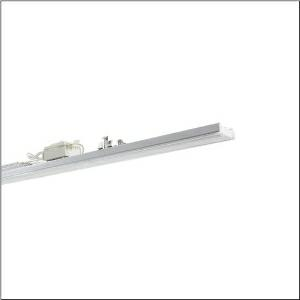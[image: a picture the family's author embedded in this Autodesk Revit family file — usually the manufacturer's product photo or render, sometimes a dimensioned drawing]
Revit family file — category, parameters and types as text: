
# Revit family: licross_21_recessed_mo_52te147n48xg
name_source: partatom
category: Lighting Fixtures
units: mm (PartAtom-declared; Revit-internal decimal feet)

## family parameters
Cut with Voids When Loaded = No
Host = Face
Light Source = No
Part Type = Normal
Room Calculation Point = No
Round Connector Dimension = Use Diameter
Shared = No

## types (1)
- Licross 21 Recessed MO (1 x LED, 8120 lm, 47.9 W, 4000K)
    Apparent Load = 48 VA
    CIE Flux Codes = 56 84 97 100 100
    Color Rendering = 80
    Color Temperature = 4000K
    Default Elevation = 1800 mm
    Description = Licross 21 Recessed MO, luminaire insert, of sheet steel, galvanised, coil coated, white, length: 1.500mm, width: 66mm, height: 67mm, LED rated luminous flux: 8.120lm, light colour: 840, SDCM (Standard Deviation of Colour Matching)MacAdam ≤ 3 SDCM (initial), control gear: ON/OFF, with plug, 3-pole, with phase selection, mains connection: 220..240V, AC, 50/60Hz, rated input power: 48W, internal wiring halogen-free, primary light control with lens, of plastic, primary optical cover: cover, of PMMA, light emission: direct distribution, primary light characteristic: asymmetric, protection rating (complete): IP54, insulation class (complete): insulation class I (protective earthing), certification: CE, ENEC, VDE, UKCA, protection symbol: D if used in an environment with non-conductive dust loads with corresponding accessories, impact resistance: IK06, permissible ambient temperature for indoor applications: -35..+40°C, corresponds to IFS (International Featured Standards) requirements for safety and quality in the food industry, reducing of maximum allowable ambient temperature of 5°C with ceiling mounting, LABS conformity tested according to VDMA 24364:2018-05, The light source and the operating device comply with the requirements of the Ecodesign Regulation (EU) 2019/2020 and are replaceable in accordance with this regulation, packaging unit: 1 piece
    Height = 58 mm
    Lamp = 1 x LED
    Lamp Light Flux = 8120 lm
    Lamp Power = 47.9 W
    Lamp count = 1
    Length = 1500 mm
    Luminous efficacy = 170 lm/W
    Manufacturer = Siteco
    ModVariant = No
    Model = 52TE147N48XG
    Mounting Place = Ceiling
    Mounting Type = Pendant
    Number of Poles = 1
    OnlyDefault = Yes
    Power Factor = 1
    Product Name = Licross 21 Recessed MO
    Product group = luminaire insert | ceiling pendant
    ProductGroupID = 901
    Protection Class = Protection class I
    Protection Degree = IP 54
    RLX_Detail_Level = 1
    RLX_Emergency_Light_Flux = 0 lm
    RLX_Emergency_Type = 0
    RLX_Emergency_Type_DB = No
    RlxData = <blob elided: 21673 chars, md5=f4212ae5>
    Socket = socket
    Standby Power = 0 W
    System Light Flux = 8120 lm
    System Power = 48 W
    Type Comments = Product without accessories
    Type Image = l_1296930.jpg
    URL = http://relux.com
    VarID = ---
    Voltage = 0 V
    Weight = 0.00 kg
    Width = 66 mm

## geometry (parser evidence)
native form markers: Blend x4, Sweep x12
no freeform markers — native parametric forms only
